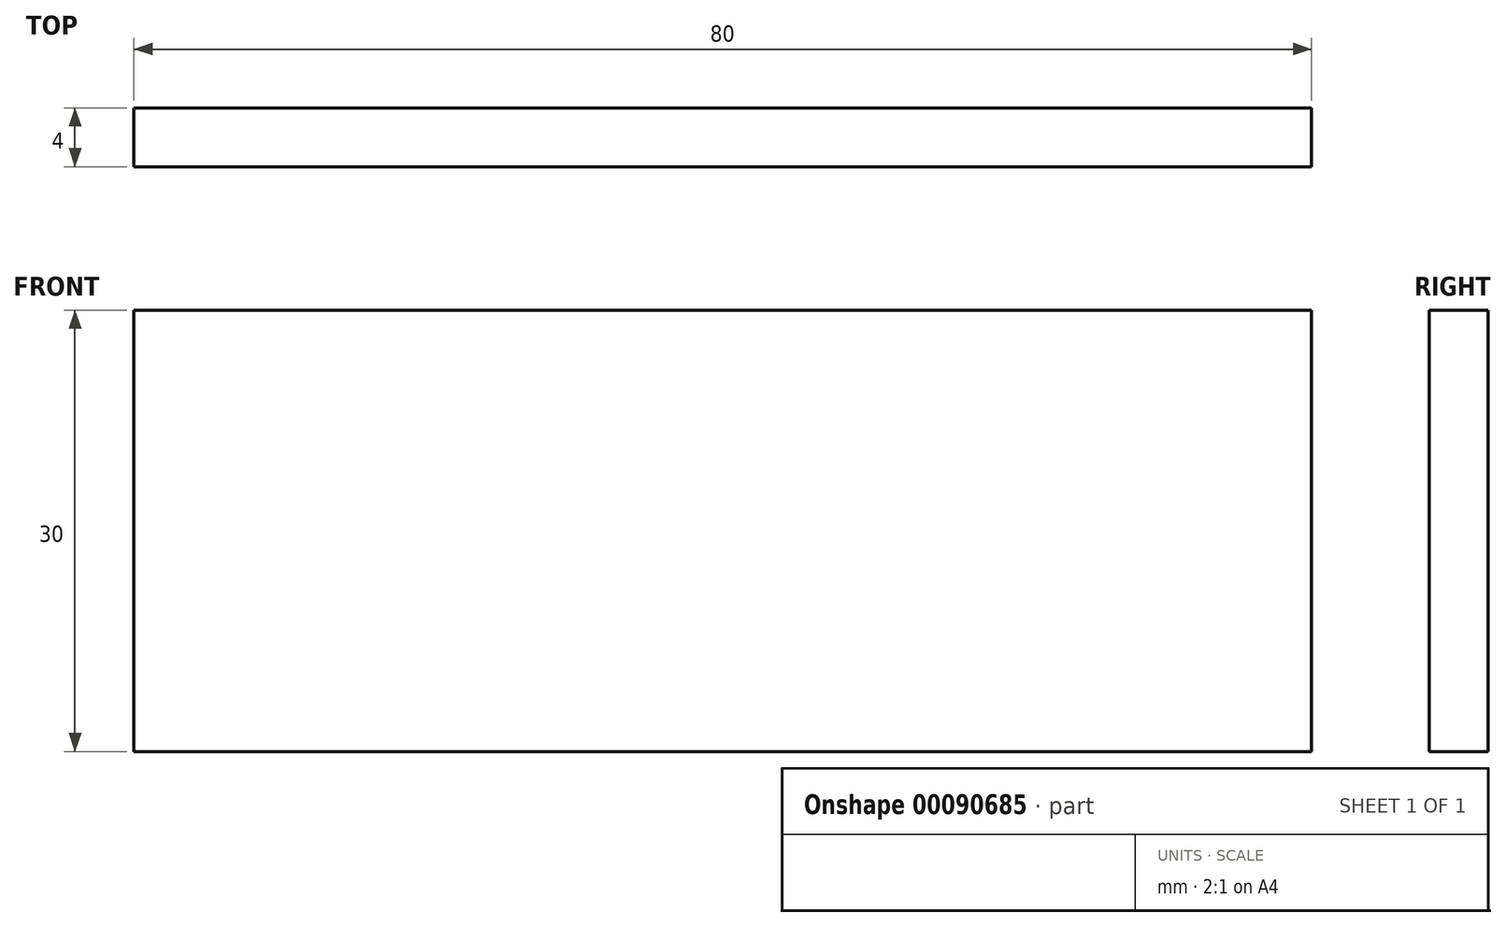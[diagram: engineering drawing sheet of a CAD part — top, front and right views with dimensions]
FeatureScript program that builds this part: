
annotation { "Feature Type Name" : "Feature", "Feature Type Description" : "" }
export const myFeature = defineFeature(function(context is Context, id is Id, definition is map)
    precondition{}
    {
        {
            var Q0;
            Q0=qCreatedBy(makeId("Front.planeOp"),FACE);
            var sketch = newSketch(context, id + "F0", { "sketchPlane" : qUnion([Q0])});
            skLineSegment(sketch, "E0.bottom", {"start": v(-42.07, -5.01) * mm, "end": v(37.93, -5.01) * mm});
            skLineSegment(sketch, "E0.top", {"start": v(-42.07, -35.01) * mm, "end": v(37.93, -35.01) * mm});
            skLineSegment(sketch, "E0.left", {"start": v(-42.07, -5.01) * mm, "end": v(-42.07, -35.01) * mm});
            skLineSegment(sketch, "E0.right", {"start": v(37.93, -5.01) * mm, "end": v(37.93, -35.01) * mm});
            skSolve(sketch);
        }
        {
            var Q0;
            Q0 = qSketchRegion(id + "F0", true);
            var Q1;
            Q1=makeQuery(id+"F0.imprint","IMPRINT",FACE,{"disambiguationData":[TD([[makeQuery(id+"F0.imprint","IMPRINT",EDGE,{"derivedFrom":sQuery(id+"F0.wireOp",EDGE,"E0.bottom")}),-1.0]])]});
            extrude(context, id + "F1", {"entities" : qUnion([Q0, Q1]), "depth" : 4 * mm});
        }
    });
